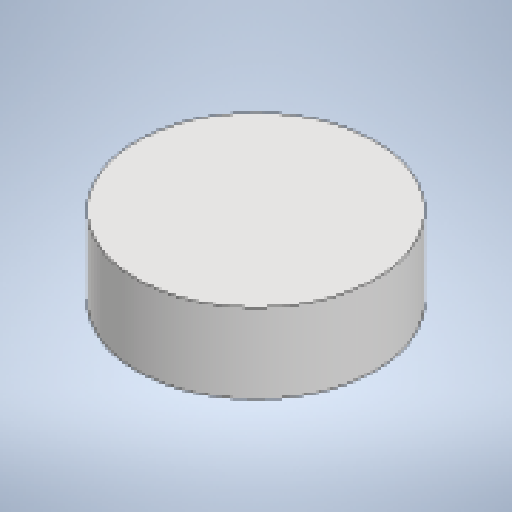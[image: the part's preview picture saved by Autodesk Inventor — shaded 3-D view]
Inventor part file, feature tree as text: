
AUTODESK INVENTOR PART (.ipt)
format: ipt  version: 2025 (Build 290162010, 162A)  size: 120,832 bytes
history: native  units: mm
features: extrude x1, sketch x1
ambient origin geometry x8: Origin, YZ Plane, XZ Plane, XY Plane, X Axis, Y Axis, Z Axis, Center Point
bodies: Solid1 (feature_tree)
feature tree (2):
  extrude  "Extrusion1"  Depth=10.0mm TaperAngle=0.0deg
  sketch  "Sketch1"  dims[d0=30.0mm d1=10.0mm d2=0.0mm]
